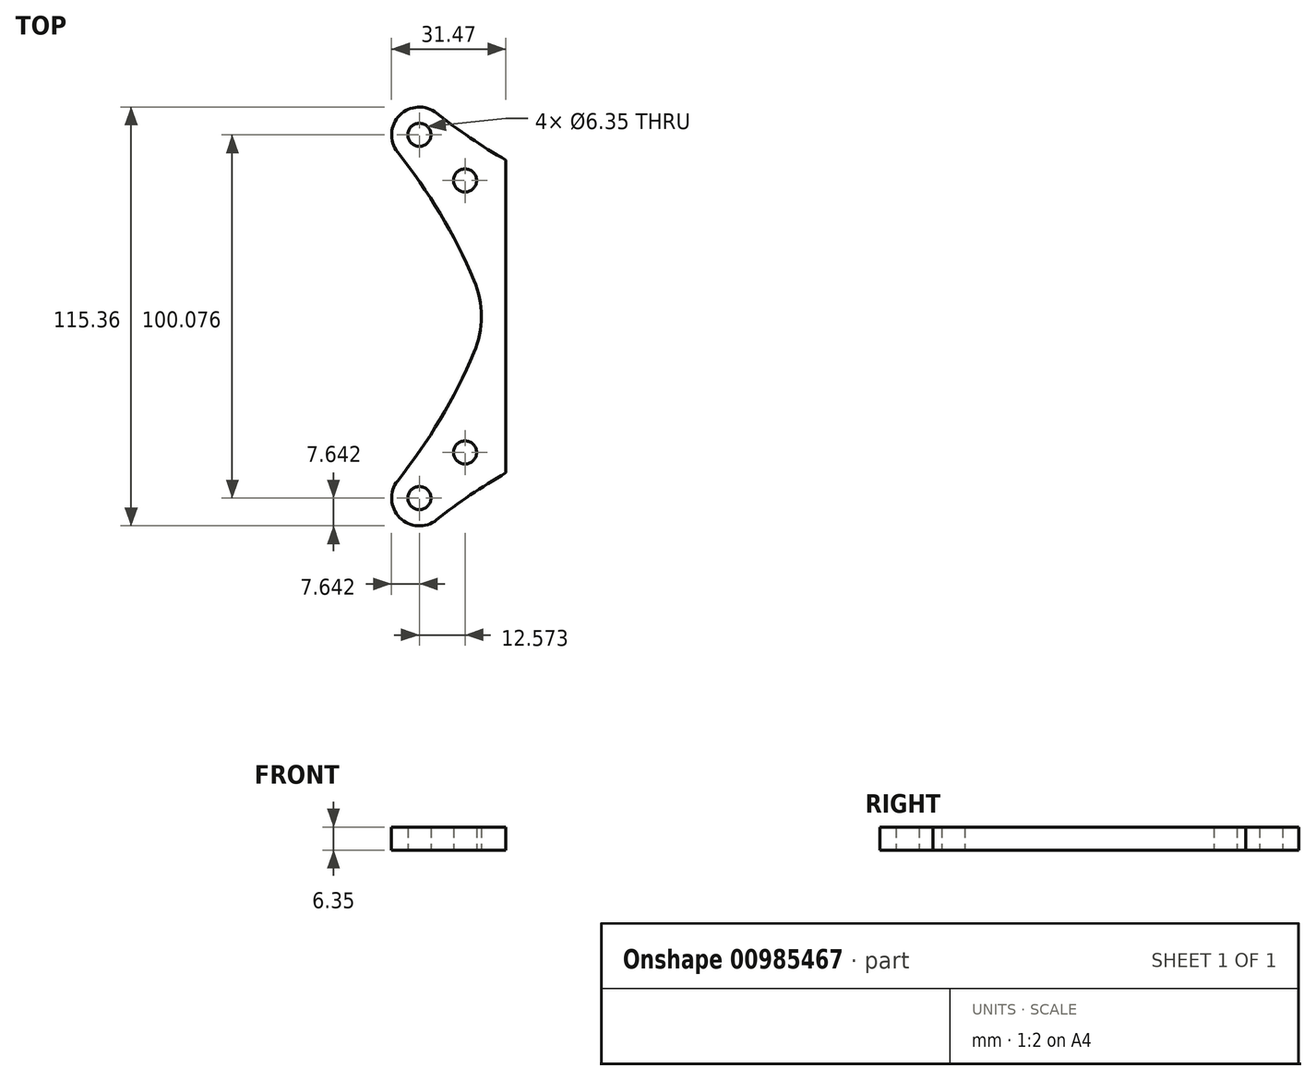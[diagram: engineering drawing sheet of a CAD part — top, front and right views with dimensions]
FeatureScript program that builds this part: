
annotation { "Feature Type Name" : "Feature", "Feature Type Description" : "" }
export const myFeature = defineFeature(function(context is Context, id is Id, definition is map)
    precondition{}
    {
        {
            var Q0;
            Q0=qCreatedBy(makeId("Top.planeOp"),FACE);
            var sketch = newSketch(context, id + "F0", { "sketchPlane" : qUnion([Q0])});
            skLineSegment(sketch, "E0.rect.bottom", {"start": v(-60.32, 60.33) * mm, "end": v(60.33, 60.33) * mm, "construction": true});
            skLineSegment(sketch, "E0.rect.left", {"start": v(-60.32, 60.33) * mm, "end": v(-60.33, -60.32) * mm, "construction": true});
            skLineSegment(sketch, "E0.rect.right", {"start": v(60.33, 60.33) * mm, "end": v(60.32, -60.32) * mm, "construction": true});
            skPoint(sketch, "E0.rect.middle", {"position": v(0, 0) * mm});
            skCircle(sketch, "E1", {"center": v(-50.04, 50.04) * mm, "radius": 3.18 * mm});
            skLineSegment(sketch, "E2", {"start": v(-50.04, 50.04) * mm, "end": v(0, 0) * mm, "construction": true});
            skCircle(sketch, "E3", {"center": v(-37.47, 37.46) * mm, "radius": 3.18 * mm});
            skCircle(sketch, "E4.MirrorC", {"center": v(-37.47, -37.46) * mm, "radius": 3.18 * mm});
            skCircle(sketch, "E5.MirrorC", {"center": v(-50.04, -50.04) * mm, "radius": 3.18 * mm});
            skLineSegment(sketch, "E6.MirrorCS", {"start": v(-50.04, -50.04) * mm, "end": v(0, 0) * mm, "construction": true});
            skCircle(sketch, "E7.MirrorC", {"center": v(37.47, 37.46) * mm, "radius": 3.18 * mm});
            skCircle(sketch, "E8.MirrorC", {"center": v(50.04, 50.04) * mm, "radius": 3.18 * mm});
            skLineSegment(sketch, "E9.MirrorCS", {"start": v(50.04, 50.04) * mm, "end": v(0, 0) * mm, "construction": true});
            skLineSegment(sketch, "E10.MirrorCS", {"start": v(50.04, -50.04) * mm, "end": v(0, 0) * mm, "construction": true});
            skCircle(sketch, "E11.MirrorC", {"center": v(37.47, -37.46) * mm, "radius": 3.18 * mm});
            skCircle(sketch, "E12.MirrorC", {"center": v(50.04, -50.04) * mm, "radius": 3.18 * mm});
            skArc(sketch, "E13", {"start": v(-45.28, 56.02) * mm, "mid": v(-55.44, 55.44) * mm, "end": v(-56.02, 45.28) * mm});
            skArc(sketch, "E14", {"start": v(-34.97, 9.93) * mm, "mid": v(-44.3, 28.32) * mm, "end": v(-56.02, 45.28) * mm});
            skArc(sketch, "E15.MirrorCS", {"start": v(-9.93, 34.97) * mm, "mid": v(-28.32, 44.3) * mm, "end": v(-45.28, 56.02) * mm});
            skArc(sketch, "E16.1.0", {"start": v(-34.97, -9.93) * mm, "mid": v(-44.3, -28.32) * mm, "end": v(-56.02, -45.28) * mm});
            skArc(sketch, "E16.1.1", {"start": v(-9.93, -34.97) * mm, "mid": v(-28.32, -44.3) * mm, "end": v(-45.28, -56.02) * mm});
            skArc(sketch, "E16.1.2", {"start": v(-56.02, -45.28) * mm, "mid": v(-55.44, -55.44) * mm, "end": v(-45.28, -56.02) * mm});
            skArc(sketch, "E16.2.0", {"start": v(9.93, -34.97) * mm, "mid": v(28.32, -44.3) * mm, "end": v(45.28, -56.02) * mm});
            skArc(sketch, "E16.2.1", {"start": v(34.97, -9.93) * mm, "mid": v(44.3, -28.32) * mm, "end": v(56.02, -45.28) * mm});
            skArc(sketch, "E16.2.2", {"start": v(45.28, -56.02) * mm, "mid": v(55.44, -55.44) * mm, "end": v(56.02, -45.28) * mm});
            skArc(sketch, "E16.3.0", {"start": v(34.97, 9.93) * mm, "mid": v(44.3, 28.32) * mm, "end": v(56.02, 45.28) * mm});
            skArc(sketch, "E16.3.1", {"start": v(9.93, 34.97) * mm, "mid": v(28.32, 44.3) * mm, "end": v(45.28, 56.02) * mm});
            skArc(sketch, "E16.3.2", {"start": v(56.02, 45.28) * mm, "mid": v(55.44, 55.44) * mm, "end": v(45.28, 56.02) * mm});
            skPoint(sketch, "E17.visualSharp", {"position": v(-31.15, 0) * mm});
            skArc(sketch, "E17.filletArc", {"start": v(-34.97, -9.93) * mm, "mid": v(-32.95, 0) * mm, "end": v(-34.97, 9.93) * mm});
            skPoint(sketch, "E18.visualSharp", {"position": v(0, 31.15) * mm});
            skArc(sketch, "E18.filletArc", {"start": v(-9.93, 34.97) * mm, "mid": v(0, 32.95) * mm, "end": v(9.93, 34.97) * mm});
            skPoint(sketch, "E19.visualSharp", {"position": v(31.15, 0) * mm});
            skArc(sketch, "E19.filletArc", {"start": v(34.97, 9.93) * mm, "mid": v(32.95, 0) * mm, "end": v(34.97, -9.93) * mm});
            skPoint(sketch, "E20.visualSharp", {"position": v(0, -31.15) * mm});
            skArc(sketch, "E20.filletArc", {"start": v(9.93, -34.97) * mm, "mid": v(0, -32.95) * mm, "end": v(-9.93, -34.97) * mm});
            skCircle(sketch, "E21", {"center": v(0, 0) * mm, "radius": 23.14 * mm, "construction": true});
            skLineSegment(sketch, "E22.bottom", {"start": v(26.2, -177.8) * mm, "end": v(-26.2, -177.8) * mm});
            skLineSegment(sketch, "E22.top", {"start": v(26.2, 177.8) * mm, "end": v(-26.2, 177.8) * mm});
            skLineSegment(sketch, "E22.left", {"start": v(26.2, -177.8) * mm, "end": v(26.2, 177.8) * mm});
            skLineSegment(sketch, "E22.right", {"start": v(-26.2, -177.8) * mm, "end": v(-26.2, 177.8) * mm});
            skCircle(sketch, "E23", {"center": v(0, 0) * mm, "radius": 177.8 * mm});
            skSolve(sketch);
        }
        {
            var Q0;
            Q0=makeQuery(id+"F0.imprint","IMPRINT",FACE,{"disambiguationData":[TD([[makeQuery(id+"F0.imprint","IMPRINT",EDGE,{"derivedFrom":sQuery(id+"F0.wireOp",EDGE,"E1")}),-1.0]])]});
            extrude(context, id + "F1", {"entities" : qUnion([Q0]), "depth" : 6.35 * mm});
        }
    });
